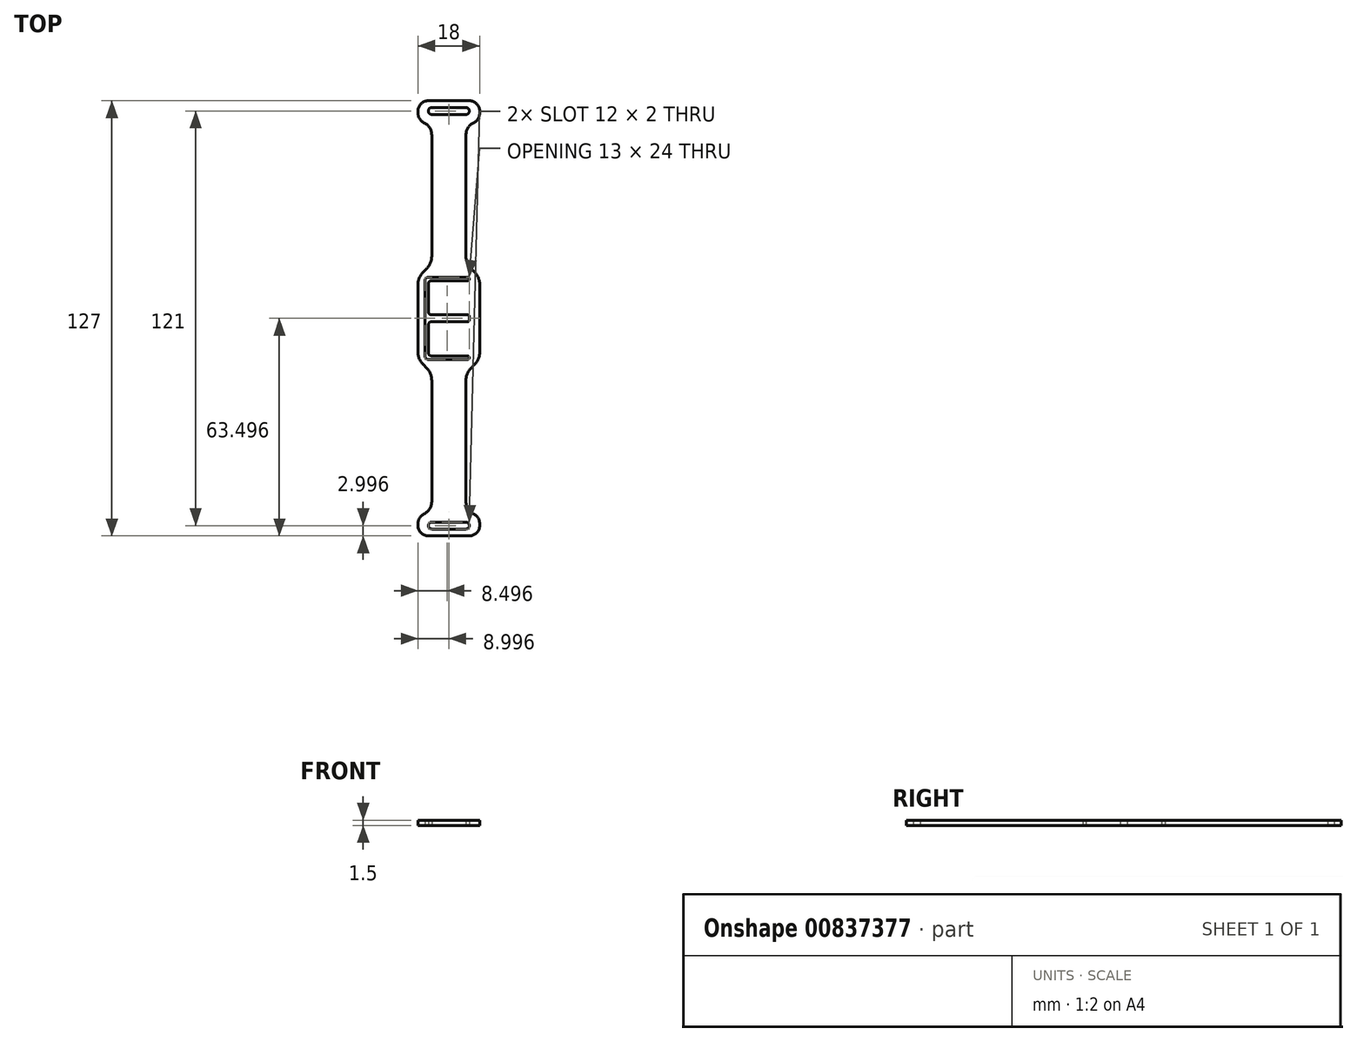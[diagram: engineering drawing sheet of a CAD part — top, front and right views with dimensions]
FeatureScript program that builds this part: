
annotation { "Feature Type Name" : "Feature", "Feature Type Description" : "" }
export const myFeature = defineFeature(function(context is Context, id is Id, definition is map)
    precondition{}
    {
        {
            var Q0;
            Q0=qCreatedBy(makeId("Top.planeOp"),FACE);
            var sketch = newSketch(context, id + "F0", { "sketchPlane" : qUnion([Q0])});
            skLineSegment(sketch, "E0.bottom", {"start": v(-3.76, 28.28) * mm, "end": v(6.74, 28.28) * mm});
            skLineSegment(sketch, "E0.top", {"start": v(-3.76, 18.28) * mm, "end": v(6.74, 18.28) * mm});
            skLineSegment(sketch, "E0.left", {"start": v(-4.76, 27.28) * mm, "end": v(-4.76, 19.28) * mm});
            skLineSegment(sketch, "E1.bottom", {"start": v(-3.76, 16.28) * mm, "end": v(6.74, 16.28) * mm});
            skLineSegment(sketch, "E1.top", {"start": v(-3.76, 6.28) * mm, "end": v(6.74, 6.28) * mm});
            skLineSegment(sketch, "E1.left", {"start": v(-4.76, 15.28) * mm, "end": v(-4.76, 7.28) * mm});
            skLineSegment(sketch, "E2.bottom", {"start": v(6.74, 29.28) * mm, "end": v(-4.76, 29.28) * mm});
            skLineSegment(sketch, "E2.left", {"start": v(7.24, 28.78) * mm, "end": v(7.24, 28.78) * mm});
            skLineSegment(sketch, "E2.right", {"start": v(-5.76, 28.28) * mm, "end": v(-5.76, 17.78) * mm});
            skLineSegment(sketch, "E3.top", {"start": v(6.74, 5.28) * mm, "end": v(-4.76, 5.28) * mm});
            skLineSegment(sketch, "E3.left", {"start": v(7.24, 16.78) * mm, "end": v(7.24, 16.28) * mm});
            skLineSegment(sketch, "E3.right", {"start": v(-5.76, 16.78) * mm, "end": v(-5.76, 6.28) * mm});
            skLineSegment(sketch, "E4.trimOffspring", {"start": v(7.24, 17.78) * mm, "end": v(7.24, 17.28) * mm});
            skLineSegment(sketch, "E5.trimOffspring", {"start": v(7.24, 5.78) * mm, "end": v(7.24, 5.78) * mm});
            skLineSegment(sketch, "E6.bottom", {"start": v(-3.76, -42.22) * mm, "end": v(6.24, -42.22) * mm});
            skLineSegment(sketch, "E6.top", {"start": v(-3.76, -44.22) * mm, "end": v(6.24, -44.22) * mm});
            skLineSegment(sketch, "E6.left", {"start": v(-4.76, -43.22) * mm, "end": v(-4.76, -43.22) * mm});
            skLineSegment(sketch, "E6.right", {"start": v(7.24, -43.22) * mm, "end": v(7.24, -43.22) * mm});
            skLineSegment(sketch, "E7.bottom", {"start": v(-3.76, 76.78) * mm, "end": v(6.24, 76.78) * mm});
            skLineSegment(sketch, "E7.top", {"start": v(-3.76, 78.78) * mm, "end": v(6.24, 78.78) * mm});
            skLineSegment(sketch, "E7.left", {"start": v(-4.76, 77.78) * mm, "end": v(-4.76, 77.78) * mm});
            skLineSegment(sketch, "E7.right", {"start": v(7.24, 77.78) * mm, "end": v(7.24, 77.78) * mm});
            skPoint(sketch, "E8.visualSharp", {"position": v(-4.76, 28.28) * mm});
            skArc(sketch, "E8.filletArc", {"start": v(-3.76, 28.28) * mm, "mid": v(-4.47, 27.98) * mm, "end": v(-4.76, 27.28) * mm});
            skPoint(sketch, "E9.visualSharp", {"position": v(-4.76, 18.28) * mm});
            skArc(sketch, "E9.filletArc", {"start": v(-4.76, 19.28) * mm, "mid": v(-4.47, 18.57) * mm, "end": v(-3.76, 18.28) * mm});
            skPoint(sketch, "E10.visualSharp", {"position": v(-5.76, 16.78) * mm});
            skPoint(sketch, "E11.visualSharp", {"position": v(-5.76, 29.28) * mm});
            skArc(sketch, "E11.filletArc", {"start": v(-4.76, 29.28) * mm, "mid": v(-5.47, 28.98) * mm, "end": v(-5.76, 28.28) * mm});
            skPoint(sketch, "E12.visualSharp", {"position": v(-4.76, 6.28) * mm});
            skArc(sketch, "E12.filletArc", {"start": v(-4.76, 7.28) * mm, "mid": v(-4.47, 6.57) * mm, "end": v(-3.76, 6.28) * mm});
            skPoint(sketch, "E13.visualSharp", {"position": v(-5.76, 5.28) * mm});
            skArc(sketch, "E13.filletArc", {"start": v(-5.76, 6.28) * mm, "mid": v(-5.47, 5.57) * mm, "end": v(-4.76, 5.28) * mm});
            skPoint(sketch, "E14.visualSharp", {"position": v(-5.76, 17.28) * mm});
            skPoint(sketch, "E15.visualSharp", {"position": v(-4.76, 16.28) * mm});
            skArc(sketch, "E15.filletArc", {"start": v(-3.76, 16.28) * mm, "mid": v(-4.47, 15.98) * mm, "end": v(-4.76, 15.28) * mm});
            skPoint(sketch, "E16.visualSharp", {"position": v(7.24, 16.28) * mm});
            skArc(sketch, "E16.filletArc", {"start": v(6.74, 16.28) * mm, "mid": v(7.09, 16.42) * mm, "end": v(7.24, 16.78) * mm});
            skPoint(sketch, "E17.visualSharp", {"position": v(7.24, 16.78) * mm});
            skPoint(sketch, "E18.visualSharp", {"position": v(7.24, 5.28) * mm});
            skArc(sketch, "E18.filletArc", {"start": v(6.74, 5.28) * mm, "mid": v(7.09, 5.42) * mm, "end": v(7.24, 5.78) * mm});
            skPoint(sketch, "E19.visualSharp", {"position": v(7.24, 6.28) * mm});
            skArc(sketch, "E19.filletArc", {"start": v(7.24, 5.78) * mm, "mid": v(7.09, 6.13) * mm, "end": v(6.74, 6.28) * mm});
            skPoint(sketch, "E20.visualSharp", {"position": v(7.24, 28.28) * mm});
            skArc(sketch, "E20.filletArc", {"start": v(6.74, 28.28) * mm, "mid": v(7.09, 28.42) * mm, "end": v(7.24, 28.78) * mm});
            skPoint(sketch, "E21.visualSharp", {"position": v(7.24, 29.28) * mm});
            skArc(sketch, "E21.filletArc", {"start": v(7.24, 28.78) * mm, "mid": v(7.09, 29.13) * mm, "end": v(6.74, 29.28) * mm});
            skPoint(sketch, "E22.visualSharp", {"position": v(7.24, 17.28) * mm});
            skPoint(sketch, "E23.visualSharp", {"position": v(7.24, 18.28) * mm});
            skArc(sketch, "E23.filletArc", {"start": v(7.24, 17.78) * mm, "mid": v(7.09, 18.13) * mm, "end": v(6.74, 18.28) * mm});
            skPoint(sketch, "E24.visualSharp", {"position": v(7.24, -42.22) * mm});
            skArc(sketch, "E24.filletArc", {"start": v(7.24, -43.22) * mm, "mid": v(6.94, -42.52) * mm, "end": v(6.24, -42.22) * mm});
            skPoint(sketch, "E25.visualSharp", {"position": v(7.24, -44.22) * mm});
            skArc(sketch, "E25.filletArc", {"start": v(6.24, -44.22) * mm, "mid": v(6.94, -43.93) * mm, "end": v(7.24, -43.22) * mm});
            skPoint(sketch, "E26.visualSharp", {"position": v(-4.76, -44.22) * mm});
            skArc(sketch, "E26.filletArc", {"start": v(-4.76, -43.22) * mm, "mid": v(-4.47, -43.93) * mm, "end": v(-3.76, -44.22) * mm});
            skPoint(sketch, "E27.visualSharp", {"position": v(-4.76, -42.22) * mm});
            skArc(sketch, "E27.filletArc", {"start": v(-3.76, -42.22) * mm, "mid": v(-4.47, -42.52) * mm, "end": v(-4.76, -43.22) * mm});
            skPoint(sketch, "E28.visualSharp", {"position": v(-4.76, 78.78) * mm});
            skArc(sketch, "E28.filletArc", {"start": v(-3.76, 78.78) * mm, "mid": v(-4.47, 78.48) * mm, "end": v(-4.76, 77.78) * mm});
            skPoint(sketch, "E29.visualSharp", {"position": v(-4.76, 76.78) * mm});
            skArc(sketch, "E29.filletArc", {"start": v(-4.76, 77.78) * mm, "mid": v(-4.47, 77.07) * mm, "end": v(-3.76, 76.78) * mm});
            skPoint(sketch, "E30.visualSharp", {"position": v(7.24, 76.78) * mm});
            skArc(sketch, "E30.filletArc", {"start": v(6.24, 76.78) * mm, "mid": v(6.94, 77.07) * mm, "end": v(7.24, 77.78) * mm});
            skPoint(sketch, "E31.visualSharp", {"position": v(7.24, 78.78) * mm});
            skArc(sketch, "E31.filletArc", {"start": v(7.24, 77.78) * mm, "mid": v(6.94, 78.48) * mm, "end": v(6.24, 78.78) * mm});
            skPoint(sketch, "E32.left.end.orphan", {"position": v(-13.76, 13.78) * mm});
            skPoint(sketch, "E32.left.start.orphan", {"position": v(-13.76, 20.78) * mm});
            skLineSegment(sketch, "E33", {"start": v(-5.76, 17.78) * mm, "end": v(-5.76, 16.78) * mm});
            skLineSegment(sketch, "E34", {"start": v(7.24, 17.28) * mm, "end": v(7.24, 16.28) * mm});
            skPoint(sketch, "E35.start.orphan", {"position": v(-13.76, 61.78) * mm});
            skPoint(sketch, "E36.start.orphan", {"position": v(-7.76, 20.78) * mm});
            skPoint(sketch, "E37.start.orphan", {"position": v(-7.76, 13.78) * mm});
            skPoint(sketch, "E38.trimOffspring.start.orphan", {"position": v(-13.76, -27.22) * mm});
            skPoint(sketch, "E39.end.orphan", {"position": v(16.24, -27.22) * mm});
            skPoint(sketch, "E40.end.orphan", {"position": v(10.24, 13.78) * mm});
            skPoint(sketch, "E41.end.orphan", {"position": v(10.24, 20.78) * mm});
            skPoint(sketch, "E42.right.end.orphan", {"position": v(16.24, 61.78) * mm});
            skPoint(sketch, "E42.bottom.start.orphan", {"position": v(-7.76, 80.78) * mm});
            skPoint(sketch, "E42.top.start.orphan", {"position": v(-13.76, -46.22) * mm});
            skLineSegment(sketch, "E43.bottom", {"start": v(-7.76, 80.78) * mm, "end": v(10.24, 80.78) * mm});
            skLineSegment(sketch, "E43.top", {"start": v(-7.76, -46.22) * mm, "end": v(10.24, -46.22) * mm});
            skLineSegment(sketch, "E43.left", {"start": v(-7.76, 80.78) * mm, "end": v(-7.76, 74.78) * mm});
            skLineSegment(sketch, "E43.right", {"start": v(10.24, 80.78) * mm, "end": v(10.24, 74.78) * mm});
            skLineSegment(sketch, "E44.bottom", {"start": v(-7.76, 74.78) * mm, "end": v(-3.76, 74.78) * mm});
            skLineSegment(sketch, "E44.top", {"start": v(-7.76, 34.28) * mm, "end": v(-3.76, 34.28) * mm});
            skLineSegment(sketch, "E44.right", {"start": v(-3.76, 74.78) * mm, "end": v(-3.76, 34.28) * mm});
            skLineSegment(sketch, "E45.bottom", {"start": v(10.24, 74.78) * mm, "end": v(6.24, 74.78) * mm});
            skLineSegment(sketch, "E45.top", {"start": v(10.24, 34.28) * mm, "end": v(6.24, 34.28) * mm});
            skLineSegment(sketch, "E45.right", {"start": v(6.24, 74.78) * mm, "end": v(6.24, 34.28) * mm});
            skLineSegment(sketch, "E46.bottom", {"start": v(-7.76, 0.28) * mm, "end": v(-3.76, 0.28) * mm});
            skLineSegment(sketch, "E46.top", {"start": v(-7.76, -40.22) * mm, "end": v(-3.76, -40.22) * mm});
            skLineSegment(sketch, "E46.right", {"start": v(-3.76, 0.28) * mm, "end": v(-3.76, -40.22) * mm});
            skLineSegment(sketch, "E47.bottom", {"start": v(10.24, 0.28) * mm, "end": v(6.24, 0.28) * mm});
            skLineSegment(sketch, "E47.top", {"start": v(10.24, -40.22) * mm, "end": v(6.24, -40.22) * mm});
            skLineSegment(sketch, "E47.right", {"start": v(6.24, 0.28) * mm, "end": v(6.24, -40.22) * mm});
            skLineSegment(sketch, "E48.trimOffspring", {"start": v(-7.76, 34.28) * mm, "end": v(-7.76, 0.28) * mm});
            skLineSegment(sketch, "E49.trimOffspring", {"start": v(10.24, 34.28) * mm, "end": v(10.24, 0.28) * mm});
            skLineSegment(sketch, "E50.trimOffspring", {"start": v(-7.76, -40.22) * mm, "end": v(-7.76, -46.22) * mm});
            skLineSegment(sketch, "E51.trimOffspring", {"start": v(10.24, -40.22) * mm, "end": v(10.24, -46.22) * mm});
            skSolve(sketch);
        }
        {
            var Q0;
            Q0=qSketchRegion(id+"F0",true);
            extrude(context, id + "F1", {"entities" : qUnion([Q0]), "depth" : 1.5 * mm, "offsetDistance" : 25 * mm});
        }
        {
            var Q0;
            Q0=makeQuery(id+"F1.opExtrude","SWEPT_EDGE",EDGE,{"disambiguationData":[OSD([sQuery(id+"F0.wireOp",EDGE,"E45.top"),sQuery(id+"F0.wireOp",EDGE,"E49.trimOffspring")])]});
            var Q1;
            Q1=makeQuery(id+"F1.opExtrude","SWEPT_EDGE",EDGE,{"disambiguationData":[OSD([sQuery(id+"F0.wireOp",EDGE,"E44.top"),sQuery(id+"F0.wireOp",EDGE,"E48.trimOffspring")])]});
            var Q2;
            Q2=makeQuery(id+"F1.opExtrude","SWEPT_EDGE",EDGE,{"disambiguationData":[OSD([sQuery(id+"F0.wireOp",EDGE,"E47.bottom"),sQuery(id+"F0.wireOp",EDGE,"E49.trimOffspring")])]});
            var Q3;
            Q3=makeQuery(id+"F1.opExtrude","SWEPT_EDGE",EDGE,{"disambiguationData":[OSD([sQuery(id+"F0.wireOp",EDGE,"E46.bottom"),sQuery(id+"F0.wireOp",EDGE,"E48.trimOffspring")])]});
            chamfer(context, id + "F2", {"entities" : qUnion([Q0, Q1, Q2, Q3]), "width" : 5 * mm, "tangentPropagation" : true});
        }
        {
            var Q0;
            {var subQ0=sQuery(id+"F0.wireOp",EDGE,"E49.trimOffspring");Q0=makeQuery(id+"F2.opChamfer","BLEND_EDGE",EDGE,{"blendedFrom":[makeQuery(id+"F1.opExtrude","SWEPT_EDGE",EDGE,{"disambiguationData":[OSD([sQuery(id+"F0.wireOp",EDGE,"E45.top"),subQ0])]}),makeQuery(id+"F1.opExtrude","SWEPT_FACE",FACE,{"disambiguationData":[OSD([subQ0])]})],"blendedInto":[makeQuery(id+"F1.opExtrude","SWEPT_FACE",FACE,{"disambiguationData":[OSD([subQ0])]})]});}
            var Q1;
            Q1=makeQuery(id+"F2.opChamfer","BLEND_EDGE",EDGE,{"blendedFrom":[makeQuery(id+"F1.opExtrude","SWEPT_EDGE",EDGE,{"disambiguationData":[OSD([sQuery(id+"F0.wireOp",EDGE,"E45.top"),sQuery(id+"F0.wireOp",EDGE,"E49.trimOffspring")])]}),makeQuery(id+"F1.opExtrude","SWEPT_FACE",FACE,{"disambiguationData":[OSD([sQuery(id+"F0.wireOp",EDGE,"E45.right")])]})],"blendedInto":[makeQuery(id+"F1.opExtrude","SWEPT_FACE",FACE,{"disambiguationData":[OSD([sQuery(id+"F0.wireOp",EDGE,"E45.right")])]})]});
            var Q2;
            Q2=makeQuery(id+"F2.opChamfer","BLEND_EDGE",EDGE,{"blendedFrom":[makeQuery(id+"F1.opExtrude","SWEPT_EDGE",EDGE,{"disambiguationData":[OSD([sQuery(id+"F0.wireOp",EDGE,"E44.top"),sQuery(id+"F0.wireOp",EDGE,"E48.trimOffspring")])]}),makeQuery(id+"F1.opExtrude","SWEPT_FACE",FACE,{"disambiguationData":[OSD([sQuery(id+"F0.wireOp",EDGE,"E44.right")])]})],"blendedInto":[makeQuery(id+"F1.opExtrude","SWEPT_FACE",FACE,{"disambiguationData":[OSD([sQuery(id+"F0.wireOp",EDGE,"E44.right")])]})]});
            var Q3;
            {var subQ0=sQuery(id+"F0.wireOp",EDGE,"E48.trimOffspring");Q3=makeQuery(id+"F2.opChamfer","BLEND_EDGE",EDGE,{"blendedFrom":[makeQuery(id+"F1.opExtrude","SWEPT_EDGE",EDGE,{"disambiguationData":[OSD([sQuery(id+"F0.wireOp",EDGE,"E44.top"),subQ0])]}),makeQuery(id+"F1.opExtrude","SWEPT_FACE",FACE,{"disambiguationData":[OSD([subQ0])]})],"blendedInto":[makeQuery(id+"F1.opExtrude","SWEPT_FACE",FACE,{"disambiguationData":[OSD([subQ0])]})]});}
            var Q4;
            {var subQ0=sQuery(id+"F0.wireOp",EDGE,"E48.trimOffspring");Q4=makeQuery(id+"F2.opChamfer","BLEND_EDGE",EDGE,{"blendedFrom":[makeQuery(id+"F1.opExtrude","SWEPT_EDGE",EDGE,{"disambiguationData":[OSD([sQuery(id+"F0.wireOp",EDGE,"E46.bottom"),subQ0])]}),makeQuery(id+"F1.opExtrude","SWEPT_FACE",FACE,{"disambiguationData":[OSD([subQ0])]})],"blendedInto":[makeQuery(id+"F1.opExtrude","SWEPT_FACE",FACE,{"disambiguationData":[OSD([subQ0])]})]});}
            var Q5;
            Q5=makeQuery(id+"F2.opChamfer","BLEND_EDGE",EDGE,{"blendedFrom":[makeQuery(id+"F1.opExtrude","SWEPT_EDGE",EDGE,{"disambiguationData":[OSD([sQuery(id+"F0.wireOp",EDGE,"E46.bottom"),sQuery(id+"F0.wireOp",EDGE,"E48.trimOffspring")])]}),makeQuery(id+"F1.opExtrude","SWEPT_FACE",FACE,{"disambiguationData":[OSD([sQuery(id+"F0.wireOp",EDGE,"E46.right")])]})],"blendedInto":[makeQuery(id+"F1.opExtrude","SWEPT_FACE",FACE,{"disambiguationData":[OSD([sQuery(id+"F0.wireOp",EDGE,"E46.right")])]})]});
            var Q6;
            Q6=makeQuery(id+"F2.opChamfer","BLEND_EDGE",EDGE,{"blendedFrom":[makeQuery(id+"F1.opExtrude","SWEPT_EDGE",EDGE,{"disambiguationData":[OSD([sQuery(id+"F0.wireOp",EDGE,"E47.bottom"),sQuery(id+"F0.wireOp",EDGE,"E49.trimOffspring")])]}),makeQuery(id+"F1.opExtrude","SWEPT_FACE",FACE,{"disambiguationData":[OSD([sQuery(id+"F0.wireOp",EDGE,"E47.right")])]})],"blendedInto":[makeQuery(id+"F1.opExtrude","SWEPT_FACE",FACE,{"disambiguationData":[OSD([sQuery(id+"F0.wireOp",EDGE,"E47.right")])]})]});
            var Q7;
            {var subQ0=sQuery(id+"F0.wireOp",EDGE,"E49.trimOffspring");Q7=makeQuery(id+"F2.opChamfer","BLEND_EDGE",EDGE,{"blendedFrom":[makeQuery(id+"F1.opExtrude","SWEPT_EDGE",EDGE,{"disambiguationData":[OSD([sQuery(id+"F0.wireOp",EDGE,"E47.bottom"),subQ0])]}),makeQuery(id+"F1.opExtrude","SWEPT_FACE",FACE,{"disambiguationData":[OSD([subQ0])]})],"blendedInto":[makeQuery(id+"F1.opExtrude","SWEPT_FACE",FACE,{"disambiguationData":[OSD([subQ0])]})]});}
            fillet(context, id + "F3", {"entities" : qUnion([Q0, Q1, Q2, Q3, Q4, Q5, Q6, Q7]), "radius" : 5 * mm, "tangentPropagation" : true, "allowEdgeOverflow" : false});
        }
        {
            var Q0;
            Q0=makeQuery(id+"F1.opExtrude","SWEPT_EDGE",EDGE,{"disambiguationData":[OSD([sQuery(id+"F0.wireOp",EDGE,"E46.top"),sQuery(id+"F0.wireOp",EDGE,"E46.right")])]});
            var Q1;
            Q1=makeQuery(id+"F1.opExtrude","SWEPT_EDGE",EDGE,{"disambiguationData":[OSD([sQuery(id+"F0.wireOp",EDGE,"E47.top"),sQuery(id+"F0.wireOp",EDGE,"E47.right")])]});
            var Q2;
            Q2=makeQuery(id+"F1.opExtrude","SWEPT_EDGE",EDGE,{"disambiguationData":[OSD([sQuery(id+"F0.wireOp",EDGE,"E44.bottom"),sQuery(id+"F0.wireOp",EDGE,"E44.right")])]});
            var Q3;
            Q3=makeQuery(id+"F1.opExtrude","SWEPT_EDGE",EDGE,{"disambiguationData":[OSD([sQuery(id+"F0.wireOp",EDGE,"E45.bottom"),sQuery(id+"F0.wireOp",EDGE,"E45.right")])]});
            fillet(context, id + "F4", {"entities" : qUnion([Q0, Q1, Q2, Q3]), "radius" : 4 * mm, "tangentPropagation" : true, "allowEdgeOverflow" : false});
        }
        {
            var Q0;
            Q0=makeQuery(id+"F1.opExtrude","SWEPT_EDGE",EDGE,{"disambiguationData":[OSD([sQuery(id+"F0.wireOp",EDGE,"E43.bottom"),sQuery(id+"F0.wireOp",EDGE,"E43.left")])]});
            var Q1;
            Q1=makeQuery(id+"F1.opExtrude","SWEPT_EDGE",EDGE,{"disambiguationData":[OSD([sQuery(id+"F0.wireOp",EDGE,"E43.bottom"),sQuery(id+"F0.wireOp",EDGE,"E43.right")])]});
            var Q2;
            Q2=makeQuery(id+"F4.opFillet","BLEND_EDGE",EDGE,{"blendedFrom":[makeQuery(id+"F1.opExtrude","SWEPT_EDGE",EDGE,{"disambiguationData":[OSD([sQuery(id+"F0.wireOp",EDGE,"E45.bottom"),sQuery(id+"F0.wireOp",EDGE,"E45.right")])]}),makeQuery(id+"F1.opExtrude","SWEPT_FACE",FACE,{"disambiguationData":[OSD([sQuery(id+"F0.wireOp",EDGE,"E43.right")])]})],"blendedInto":[makeQuery(id+"F1.opExtrude","SWEPT_FACE",FACE,{"disambiguationData":[OSD([sQuery(id+"F0.wireOp",EDGE,"E43.right")])]})]});
            var Q3;
            Q3=makeQuery(id+"F4.opFillet","BLEND_EDGE",EDGE,{"blendedFrom":[makeQuery(id+"F1.opExtrude","SWEPT_EDGE",EDGE,{"disambiguationData":[OSD([sQuery(id+"F0.wireOp",EDGE,"E44.bottom"),sQuery(id+"F0.wireOp",EDGE,"E44.right")])]}),makeQuery(id+"F1.opExtrude","SWEPT_FACE",FACE,{"disambiguationData":[OSD([sQuery(id+"F0.wireOp",EDGE,"E43.left")])]})],"blendedInto":[makeQuery(id+"F1.opExtrude","SWEPT_FACE",FACE,{"disambiguationData":[OSD([sQuery(id+"F0.wireOp",EDGE,"E43.left")])]})]});
            var Q4;
            Q4=makeQuery(id+"F1.opExtrude","SWEPT_EDGE",EDGE,{"disambiguationData":[OSD([sQuery(id+"F0.wireOp",EDGE,"E43.top"),sQuery(id+"F0.wireOp",EDGE,"E50.trimOffspring")])]});
            var Q5;
            Q5=makeQuery(id+"F4.opFillet","BLEND_EDGE",EDGE,{"blendedFrom":[makeQuery(id+"F1.opExtrude","SWEPT_EDGE",EDGE,{"disambiguationData":[OSD([sQuery(id+"F0.wireOp",EDGE,"E46.top"),sQuery(id+"F0.wireOp",EDGE,"E46.right")])]}),makeQuery(id+"F1.opExtrude","SWEPT_FACE",FACE,{"disambiguationData":[OSD([sQuery(id+"F0.wireOp",EDGE,"E50.trimOffspring")])]})],"blendedInto":[makeQuery(id+"F1.opExtrude","SWEPT_FACE",FACE,{"disambiguationData":[OSD([sQuery(id+"F0.wireOp",EDGE,"E50.trimOffspring")])]})]});
            var Q6;
            Q6=makeQuery(id+"F4.opFillet","BLEND_EDGE",EDGE,{"blendedFrom":[makeQuery(id+"F1.opExtrude","SWEPT_EDGE",EDGE,{"disambiguationData":[OSD([sQuery(id+"F0.wireOp",EDGE,"E47.top"),sQuery(id+"F0.wireOp",EDGE,"E47.right")])]}),makeQuery(id+"F1.opExtrude","SWEPT_FACE",FACE,{"disambiguationData":[OSD([sQuery(id+"F0.wireOp",EDGE,"E51.trimOffspring")])]})],"blendedInto":[makeQuery(id+"F1.opExtrude","SWEPT_FACE",FACE,{"disambiguationData":[OSD([sQuery(id+"F0.wireOp",EDGE,"E51.trimOffspring")])]})]});
            var Q7;
            Q7=makeQuery(id+"F1.opExtrude","SWEPT_EDGE",EDGE,{"disambiguationData":[OSD([sQuery(id+"F0.wireOp",EDGE,"E43.top"),sQuery(id+"F0.wireOp",EDGE,"E51.trimOffspring")])]});
            fillet(context, id + "F5", {"entities" : qUnion([Q0, Q1, Q2, Q3, Q4, Q5, Q6, Q7]), "radius" : 3 * mm, "tangentPropagation" : true, "allowEdgeOverflow" : false});
        }
    });
